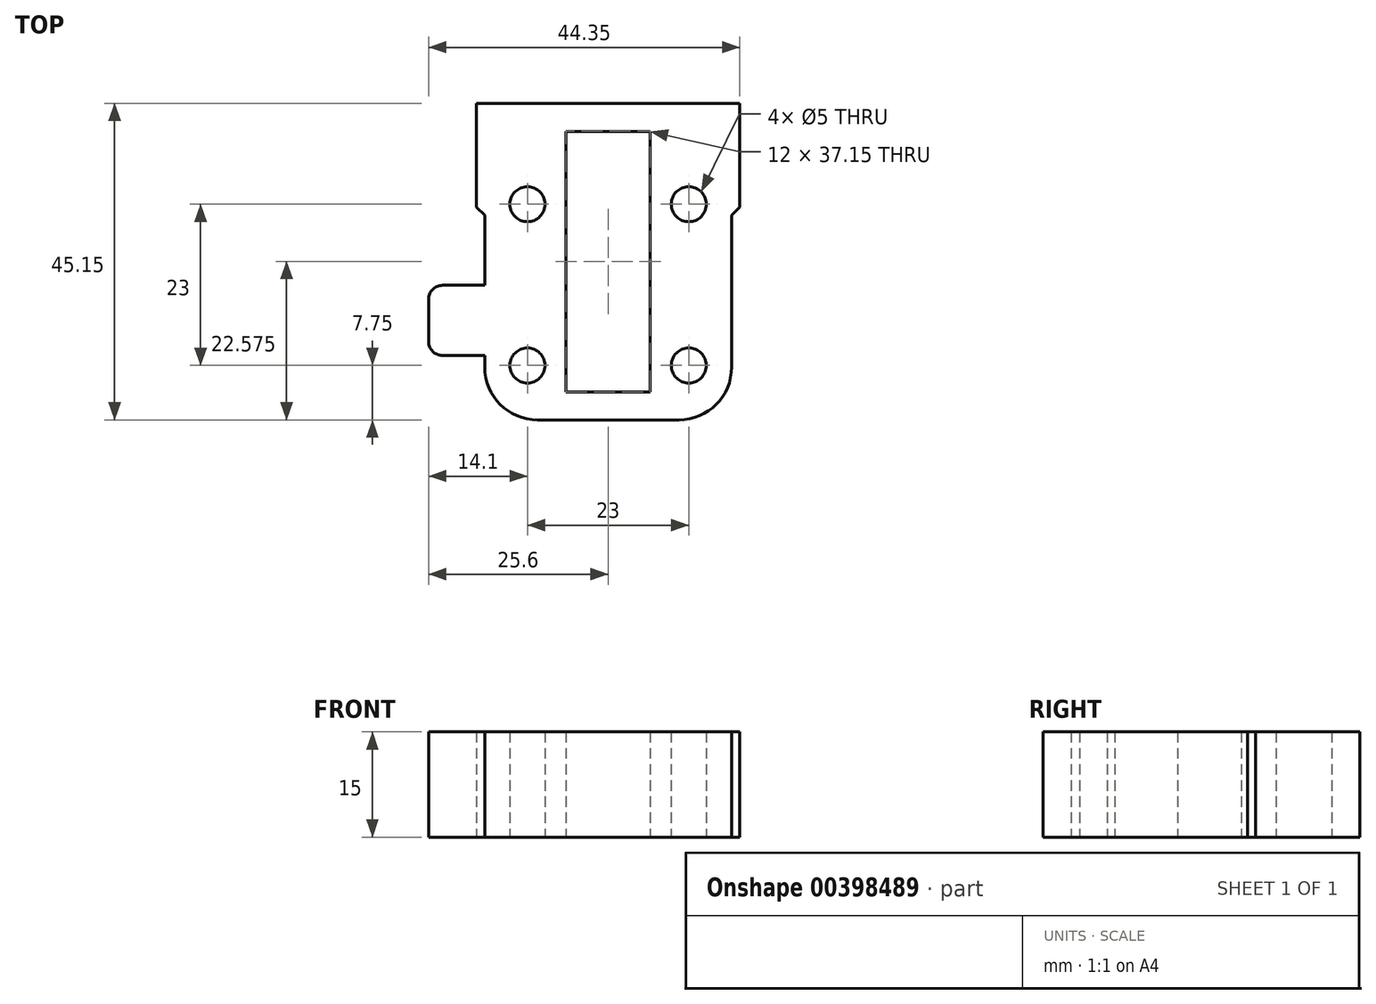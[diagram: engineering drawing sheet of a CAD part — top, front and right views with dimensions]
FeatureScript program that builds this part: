
annotation { "Feature Type Name" : "Feature", "Feature Type Description" : "" }
export const myFeature = defineFeature(function(context is Context, id is Id, definition is map)
    precondition{}
    {
        {
            var Q0;
            Q0=qCreatedBy(makeId("Top.planeOp"),FACE);
            var sketch = newSketch(context, id + "F0", { "sketchPlane" : qUnion([Q0])});
            skLineSegment(sketch, "E0.0", {"start": v(8.95, 45.15) * mm, "end": v(8.95, 30.3) * mm});
            skLineSegment(sketch, "E1.0", {"start": v(46.45, 45.15) * mm, "end": v(8.95, 45.15) * mm});
            skLineSegment(sketch, "E2.0", {"start": v(46.45, 30.3) * mm, "end": v(46.45, 45.15) * mm});
            skLineSegment(sketch, "E3.0", {"start": v(21.7, 41.15) * mm, "end": v(33.7, 41.15) * mm});
            skLineSegment(sketch, "E4.0", {"start": v(33.7, 41.15) * mm, "end": v(33.7, 4) * mm});
            skLineSegment(sketch, "E5.0", {"start": v(21.7, 4) * mm, "end": v(21.7, 41.15) * mm});
            skLineSegment(sketch, "E6.0", {"start": v(33.7, 4) * mm, "end": v(21.7, 4) * mm});
            skLineSegment(sketch, "E7.0", {"start": v(17.6, 0) * mm, "end": v(37.8, 0) * mm});
            skLineSegment(sketch, "E8.0", {"start": v(10.1, 29.15) * mm, "end": v(10.1, 7.5) * mm});
            skLineSegment(sketch, "E9.0", {"start": v(45.3, 7.5) * mm, "end": v(45.3, 29.15) * mm});
            skPoint(sketch, "E10.0", {"position": v(16.1, 33.25) * mm});
            skPoint(sketch, "E11.0", {"position": v(13.84, 29.92) * mm});
            skPoint(sketch, "E12.0", {"position": v(18, 29.02) * mm});
            skPoint(sketch, "E13", {"position": v(27.7, 45.15) * mm});
            skArc(sketch, "E14.filletArc", {"start": v(10.1, 7.5) * mm, "mid": v(12.3, 2.2) * mm, "end": v(17.6, 0) * mm});
            skPoint(sketch, "E15.newPointB", {"position": v(37.8, 0) * mm});
            skArc(sketch, "E15.filletArc", {"start": v(37.8, 0) * mm, "mid": v(43.1, 2.2) * mm, "end": v(45.3, 7.5) * mm});
            skLineSegment(sketch, "E16", {"start": v(8.95, 30.3) * mm, "end": v(10.1, 29.15) * mm});
            skLineSegment(sketch, "E17", {"start": v(46.45, 30.3) * mm, "end": v(45.3, 29.15) * mm});
            skCircle(sketch, "E18", {"center": v(16.2, 30.75) * mm, "radius": 2.5 * mm});
            skCircle(sketch, "E19", {"center": v(16.2, 7.75) * mm, "radius": 2.5 * mm});
            skCircle(sketch, "E20", {"center": v(39.2, 30.75) * mm, "radius": 2.5 * mm});
            skCircle(sketch, "E21", {"center": v(39.2, 7.75) * mm, "radius": 2.5 * mm});
            skSolve(sketch);
        }
        {
            var Q0;
            Q0 = qSketchRegion(id + "F0", true);
            extrude(context, id + "F1", {"entities" : qUnion([Q0]), "depth" : 15 * mm});
        }
        {
            var Q0;
            Q0=makeQuery(id+"F1.opExtrude","SWEPT_FACE",FACE,{"disambiguationData":[OSD([sQuery(id+"F0.wireOp",EDGE,"E8.0")])]});
            var sketch = newSketch(context, id + "F2", { "sketchPlane" : qUnion([Q0])});
            skLineSegment(sketch, "E22.0", {"start": v(0, 15) * mm, "end": v(0, 0) * mm, "construction": true});
            skPoint(sketch, "E23.0", {"position": v(-18.33, 0) * mm});
            skLineSegment(sketch, "E24.bottom", {"start": v(-19.18, 15) * mm, "end": v(-9.18, 15) * mm});
            skLineSegment(sketch, "E24.top", {"start": v(-19.18, 0) * mm, "end": v(-9.18, 0) * mm});
            skLineSegment(sketch, "E24.left", {"start": v(-19.18, 15) * mm, "end": v(-19.18, 0) * mm});
            skLineSegment(sketch, "E24.right", {"start": v(-9.18, 15) * mm, "end": v(-9.18, 0) * mm});
            skSolve(sketch);
        }
        {
            var Q0;
            Q0 = qSketchRegion(id + "F2", true);
            extrude(context, id + "F3", {"entities" : qUnion([Q0]), "operationType" : NewBodyOperationType.ADD, "depth" : 8 * mm});
        }
        {
            var Q0;
            Q0=makeQuery(id+"F3.opExtrude","CAP_EDGE",EDGE,{"disambiguationData":[OSD([sQuery(id+"F2.wireOp",EDGE,"E24.left")])],"isStart":false});
            var Q1;
            Q1=makeQuery(id+"F3.opExtrude","CAP_EDGE",EDGE,{"disambiguationData":[OSD([sQuery(id+"F2.wireOp",EDGE,"E24.right")])],"isStart":false});
            fillet(context, id + "F4", {"entities" : qUnion([Q0, Q1]), "radius" : 2 * mm, "tangentPropagation" : true, "allowEdgeOverflow" : false});
        }
    });
